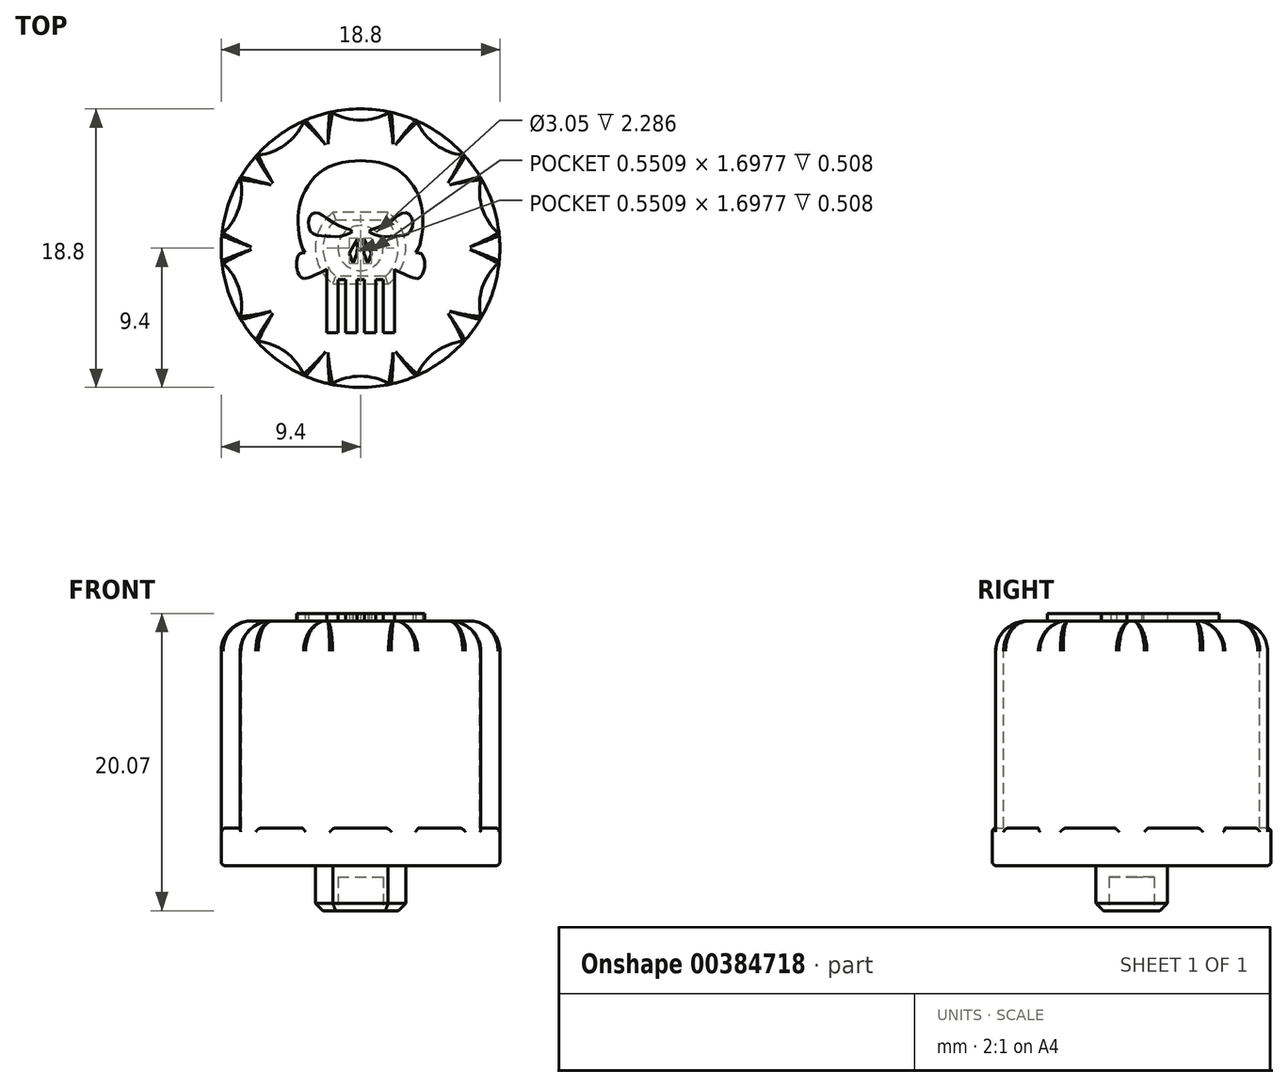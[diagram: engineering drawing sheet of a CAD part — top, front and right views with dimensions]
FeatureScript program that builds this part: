
annotation { "Feature Type Name" : "Feature", "Feature Type Description" : "" }
export const myFeature = defineFeature(function(context is Context, id is Id, definition is map)
    precondition{}
    {
        {
            var Q0;
            Q0=qCreatedBy(makeId("Top.planeOp"),FACE);
            var sketch = newSketch(context, id + "F0", { "sketchPlane" : qUnion([Q0])});
            skCircle(sketch, "E0", {"center": v(0, 0) * mm, "radius": 9.4 * mm});
            skSolve(sketch);
        }
        {
            var Q0;
            Q0=qSketchRegion(id+"F0",true);
            extrude(context, id + "F1", {"entities" : qUnion([Q0]), "depth" : 16.5 * mm});
        }
        {
            var Q0;
            Q0=makeQuery(id+"F1.opExtrude","CAP_FACE",FACE,{"disambiguationData":[OSD([sQuery(id+"F0.wireOp",EDGE,"E0")])],"isStart":false});
            var sketch = newSketch(context, id + "F2", { "sketchPlane" : qUnion([Q0])});
            skCircle(sketch, "E1.1.0", {"center": v(-7.32, 10.07) * mm, "radius": 3.81 * mm});
            skCircle(sketch, "E1.2.0", {"center": v(-11.84, 3.85) * mm, "radius": 3.81 * mm});
            skCircle(sketch, "E1.3.0", {"center": v(-11.84, -3.85) * mm, "radius": 3.81 * mm});
            skCircle(sketch, "E1.4.0", {"center": v(-7.32, -10.07) * mm, "radius": 3.81 * mm});
            skCircle(sketch, "E1.5.0", {"center": v(0, -12.45) * mm, "radius": 3.81 * mm});
            skCircle(sketch, "E1.6.0", {"center": v(7.32, -10.07) * mm, "radius": 3.81 * mm});
            skCircle(sketch, "E1.7.0", {"center": v(11.84, -3.85) * mm, "radius": 3.81 * mm});
            skCircle(sketch, "E1.8.0", {"center": v(11.84, 3.85) * mm, "radius": 3.81 * mm});
            skCircle(sketch, "E1.9.0", {"center": v(7.32, 10.07) * mm, "radius": 3.81 * mm});
            skPoint(sketch, "E1.center", {"position": v(0, 0) * mm});
            skPoint(sketch, "E2.center.orphan", {"position": v(0, 12.45) * mm});
            skCircle(sketch, "E3", {"center": v(0, 12.45) * mm, "radius": 3.81 * mm});
            skSolve(sketch);
        }
        {
            var Q0;
            Q0=qSketchRegion(id+"F2",true);
            extrude(context, id + "F3", {"entities" : qUnion([Q0]), "operationType" : NewBodyOperationType.REMOVE, "oppositeDirection" : true, "depth" : 13.97 * mm});
        }
        {
            var Q0;
            Q0=makeQuery(id+"F1.opExtrude","CAP_FACE",FACE,{"disambiguationData":[OSD([sQuery(id+"F0.wireOp",EDGE,"E0")])],"isStart":false});
            fillet(context, id + "F4", {"entities" : qUnion([Q0]), "radius" : 2.03 * mm, "tangentPropagation" : true, "allowEdgeOverflow" : false});
        }
        {
            var Q0;
            Q0=makeQuery(id+"F1.opExtrude","CAP_FACE",FACE,{"disambiguationData":[OSD([sQuery(id+"F0.wireOp",EDGE,"E0")])],"isStart":true});
            var sketch = newSketch(context, id + "F5", { "sketchPlane" : qUnion([Q0])});
            skCircle(sketch, "E4", {"center": v(0, 0) * mm, "radius": 5.33 * mm});
            skSolve(sketch);
        }
        {
            var Q0;
            Q0=qSketchRegion(id+"F5",true);
            extrude(context, id + "F6", {"entities" : qUnion([Q0]), "operationType" : NewBodyOperationType.ADD, "depth" : 8.25 * mm, "offsetDistance" : 25.4 * mm});
        }
        {
            var Q0;
            Q0=makeQuery(id+"F6.opExtrude","CAP_FACE",FACE,{"disambiguationData":[OSD([sQuery(id+"F5.wireOp",EDGE,"E4")])],"isStart":false});
            var sketch = newSketch(context, id + "F7", { "sketchPlane" : qUnion([Q0])});
            skCircle(sketch, "E5", {"center": v(0, 10.16) * mm, "radius": 5.72 * mm});
            skCircle(sketch, "E6.1.0", {"center": v(-9.66, 3.14) * mm, "radius": 5.72 * mm});
            skCircle(sketch, "E6.2.0", {"center": v(-5.97, -8.22) * mm, "radius": 5.72 * mm});
            skCircle(sketch, "E6.3.0", {"center": v(5.97, -8.22) * mm, "radius": 5.72 * mm});
            skCircle(sketch, "E6.4.0", {"center": v(9.66, 3.14) * mm, "radius": 5.72 * mm});
            skPoint(sketch, "E6.center", {"position": v(0, 0) * mm});
            skSolve(sketch);
        }
        {
            var Q0;
            Q0=qSketchRegion(id+"F7",true);
            extrude(context, id + "F8", {"entities" : qUnion([Q0]), "operationType" : NewBodyOperationType.REMOVE, "oppositeDirection" : true, "depth" : 7.62 * mm});
        }
        {
            var Q0;
            Q0=makeQuery(id+"F8.boolean.opBoolean","MERGE",FACE,{"derivedFrom":[makeQuery(id+"F1.opExtrude","CAP_FACE",FACE,{"disambiguationData":[OSD([sQuery(id+"F0.wireOp",EDGE,"E0")])],"isStart":true}),makeQuery(id+"F8.opExtrude","CAP_FACE",FACE,{"disambiguationData":[OSD([sQuery(id+"F7.wireOp",EDGE,"E5")])],"isStart":false}),makeQuery(id+"F8.opExtrude","CAP_FACE",FACE,{"disambiguationData":[OSD([sQuery(id+"F7.wireOp",EDGE,"E6.1.0")])],"isStart":false}),makeQuery(id+"F8.opExtrude","CAP_FACE",FACE,{"disambiguationData":[OSD([sQuery(id+"F7.wireOp",EDGE,"E6.2.0")])],"isStart":false}),makeQuery(id+"F8.opExtrude","CAP_FACE",FACE,{"disambiguationData":[OSD([sQuery(id+"F7.wireOp",EDGE,"E6.3.0")])],"isStart":false}),makeQuery(id+"F8.opExtrude","CAP_FACE",FACE,{"disambiguationData":[OSD([sQuery(id+"F7.wireOp",EDGE,"E6.4.0")])],"isStart":false})]});
            var sketch = newSketch(context, id + "F9", { "sketchPlane" : qUnion([Q0])});
            skCircle(sketch, "E7", {"center": v(0, 0) * mm, "radius": 6.22 * mm});
            skCircle(sketch, "E8", {"center": v(0, 0) * mm, "radius": 4.32 * mm});
            skSolve(sketch);
        }
        {
            var Q0;
            Q0=qSketchRegion(id+"F9",true);
            extrude(context, id + "F10", {"entities" : qUnion([Q0]), "operationType" : NewBodyOperationType.REMOVE, "depth" : 4.06 * mm, "offsetDistance" : 25.4 * mm});
        }
        {
            var Q0;
            Q0=makeQuery(id+"F10.boolean.opBoolean","MERGE",FACE,{"derivedFrom":[makeQuery(id+"F1.opExtrude","CAP_FACE",FACE,{"disambiguationData":[OSD([sQuery(id+"F0.wireOp",EDGE,"E0")])],"isStart":true}),makeQuery(id+"F10.opExtrude","CAP_FACE",FACE,{"disambiguationData":[OSD([sQuery(id+"F9.wireOp",EDGE,"E7"),sQuery(id+"F9.wireOp",EDGE,"E8")])],"isStart":true})]});
            var sketch = newSketch(context, id + "F11", { "sketchPlane" : qUnion([Q0])});
            skCircle(sketch, "E9", {"center": v(0, 0) * mm, "radius": 6.35 * mm});
            skSolve(sketch);
        }
        {
            var Q0;
            Q0=qSketchRegion(id+"F11",true);
            extrude(context, id + "F12", {"entities" : qUnion([Q0]), "operationType" : NewBodyOperationType.ADD, "depth" : 2.54 * mm, "offsetDistance" : 25.4 * mm});
        }
        {
            var Q0;
            Q0=makeQuery(id+"F6.opExtrude","CAP_FACE",FACE,{"disambiguationData":[OSD([sQuery(id+"F5.wireOp",EDGE,"E4")])],"isStart":false});
            fillet(context, id + "F13", {"entities" : qUnion([Q0]), "radius" : 0.5 * mm, "tangentPropagation" : true, "allowEdgeOverflow" : false});
        }
        {
            var Q0;
            Q0=makeQuery(id+"F12.opExtrude","CAP_EDGE",EDGE,{"disambiguationData":[OSD([sQuery(id+"F11.wireOp",EDGE,"E9")])],"isStart":false});
            var Q1;
            Q1=makeQuery(id+"F1.opExtrude","CAP_EDGE",EDGE,{"disambiguationData":[OSD([sQuery(id+"F0.wireOp",EDGE,"E0")])],"isStart":true});
            var Q2;
            Q2=makeQuery(id+"F3.boolean.opBoolean","INTERSECT",EDGE,{"derivedFrom":[makeQuery(id+"F1.opExtrude","SWEPT_FACE",FACE,{"disambiguationData":[OSD([sQuery(id+"F0.wireOp",EDGE,"E0")])]}),makeQuery(id+"F3.opExtrude","CAP_FACE",FACE,{"disambiguationData":[OSD([sQuery(id+"F2.wireOp",EDGE,"E1.4.0")])],"isStart":false})]});
            var Q3;
            Q3=makeQuery(id+"F3.boolean.opBoolean","INTERSECT",EDGE,{"derivedFrom":[makeQuery(id+"F1.opExtrude","SWEPT_FACE",FACE,{"disambiguationData":[OSD([sQuery(id+"F0.wireOp",EDGE,"E0")])]}),makeQuery(id+"F3.opExtrude","CAP_FACE",FACE,{"disambiguationData":[OSD([sQuery(id+"F2.wireOp",EDGE,"E1.5.0")])],"isStart":false})]});
            var Q4;
            Q4=makeQuery(id+"F3.boolean.opBoolean","INTERSECT",EDGE,{"disambiguationData":[OD(0.0)],"derivedFrom":[makeQuery(id+"F1.opExtrude","SWEPT_FACE",FACE,{"disambiguationData":[OSD([sQuery(id+"F0.wireOp",EDGE,"E0")])]}),makeQuery(id+"F3.opExtrude","SWEPT_FACE",FACE,{"disambiguationData":[OSD([sQuery(id+"F2.wireOp",EDGE,"E1.4.0")])]})]});
            var Q5;
            Q5=makeQuery(id+"F3.boolean.opBoolean","INTERSECT",EDGE,{"disambiguationData":[OD(1.0)],"derivedFrom":[makeQuery(id+"F1.opExtrude","SWEPT_FACE",FACE,{"disambiguationData":[OSD([sQuery(id+"F0.wireOp",EDGE,"E0")])]}),makeQuery(id+"F3.opExtrude","SWEPT_FACE",FACE,{"disambiguationData":[OSD([sQuery(id+"F2.wireOp",EDGE,"E1.4.0")])]})]});
            var Q6;
            Q6=makeQuery(id+"F3.boolean.opBoolean","INTERSECT",EDGE,{"disambiguationData":[OD(0.0)],"derivedFrom":[makeQuery(id+"F1.opExtrude","SWEPT_FACE",FACE,{"disambiguationData":[OSD([sQuery(id+"F0.wireOp",EDGE,"E0")])]}),makeQuery(id+"F3.opExtrude","SWEPT_FACE",FACE,{"disambiguationData":[OSD([sQuery(id+"F2.wireOp",EDGE,"E1.5.0")])]})]});
            var Q7;
            Q7=makeQuery(id+"F3.boolean.opBoolean","INTERSECT",EDGE,{"disambiguationData":[OD(1.0)],"derivedFrom":[makeQuery(id+"F1.opExtrude","SWEPT_FACE",FACE,{"disambiguationData":[OSD([sQuery(id+"F0.wireOp",EDGE,"E0")])]}),makeQuery(id+"F3.opExtrude","SWEPT_FACE",FACE,{"disambiguationData":[OSD([sQuery(id+"F2.wireOp",EDGE,"E1.5.0")])]})]});
            var Q8;
            Q8=makeQuery(id+"F3.boolean.opBoolean","INTERSECT",EDGE,{"disambiguationData":[OD(0.0)],"derivedFrom":[makeQuery(id+"F1.opExtrude","SWEPT_FACE",FACE,{"disambiguationData":[OSD([sQuery(id+"F0.wireOp",EDGE,"E0")])]}),makeQuery(id+"F3.opExtrude","SWEPT_FACE",FACE,{"disambiguationData":[OSD([sQuery(id+"F2.wireOp",EDGE,"E1.6.0")])]})]});
            var Q9;
            Q9=makeQuery(id+"F3.boolean.opBoolean","INTERSECT",EDGE,{"derivedFrom":[makeQuery(id+"F1.opExtrude","SWEPT_FACE",FACE,{"disambiguationData":[OSD([sQuery(id+"F0.wireOp",EDGE,"E0")])]}),makeQuery(id+"F3.opExtrude","CAP_FACE",FACE,{"disambiguationData":[OSD([sQuery(id+"F2.wireOp",EDGE,"E1.6.0")])],"isStart":false})]});
            var Q10;
            Q10=makeQuery(id+"F3.boolean.opBoolean","INTERSECT",EDGE,{"disambiguationData":[OD(1.0)],"derivedFrom":[makeQuery(id+"F1.opExtrude","SWEPT_FACE",FACE,{"disambiguationData":[OSD([sQuery(id+"F0.wireOp",EDGE,"E0")])]}),makeQuery(id+"F3.opExtrude","SWEPT_FACE",FACE,{"disambiguationData":[OSD([sQuery(id+"F2.wireOp",EDGE,"E1.6.0")])]})]});
            var Q11;
            Q11=makeQuery(id+"F3.boolean.opBoolean","INTERSECT",EDGE,{"disambiguationData":[OD(0.0)],"derivedFrom":[makeQuery(id+"F1.opExtrude","SWEPT_FACE",FACE,{"disambiguationData":[OSD([sQuery(id+"F0.wireOp",EDGE,"E0")])]}),makeQuery(id+"F3.opExtrude","SWEPT_FACE",FACE,{"disambiguationData":[OSD([sQuery(id+"F2.wireOp",EDGE,"E1.7.0")])]})]});
            var Q12;
            Q12=makeQuery(id+"F3.boolean.opBoolean","INTERSECT",EDGE,{"derivedFrom":[makeQuery(id+"F1.opExtrude","SWEPT_FACE",FACE,{"disambiguationData":[OSD([sQuery(id+"F0.wireOp",EDGE,"E0")])]}),makeQuery(id+"F3.opExtrude","CAP_FACE",FACE,{"disambiguationData":[OSD([sQuery(id+"F2.wireOp",EDGE,"E1.7.0")])],"isStart":false})]});
            var Q13;
            Q13=makeQuery(id+"F3.boolean.opBoolean","INTERSECT",EDGE,{"disambiguationData":[OD(1.0)],"derivedFrom":[makeQuery(id+"F1.opExtrude","SWEPT_FACE",FACE,{"disambiguationData":[OSD([sQuery(id+"F0.wireOp",EDGE,"E0")])]}),makeQuery(id+"F3.opExtrude","SWEPT_FACE",FACE,{"disambiguationData":[OSD([sQuery(id+"F2.wireOp",EDGE,"E1.7.0")])]})]});
            var Q14;
            Q14=makeQuery(id+"F3.boolean.opBoolean","INTERSECT",EDGE,{"derivedFrom":[makeQuery(id+"F1.opExtrude","SWEPT_FACE",FACE,{"disambiguationData":[OSD([sQuery(id+"F0.wireOp",EDGE,"E0")])]}),makeQuery(id+"F3.opExtrude","CAP_FACE",FACE,{"disambiguationData":[OSD([sQuery(id+"F2.wireOp",EDGE,"E1.8.0")])],"isStart":false})]});
            var Q15;
            Q15=makeQuery(id+"F3.boolean.opBoolean","INTERSECT",EDGE,{"disambiguationData":[OD(0.0)],"derivedFrom":[makeQuery(id+"F1.opExtrude","SWEPT_FACE",FACE,{"disambiguationData":[OSD([sQuery(id+"F0.wireOp",EDGE,"E0")])]}),makeQuery(id+"F3.opExtrude","SWEPT_FACE",FACE,{"disambiguationData":[OSD([sQuery(id+"F2.wireOp",EDGE,"E1.8.0")])]})]});
            var Q16;
            Q16=makeQuery(id+"F3.boolean.opBoolean","INTERSECT",EDGE,{"disambiguationData":[OD(1.0)],"derivedFrom":[makeQuery(id+"F1.opExtrude","SWEPT_FACE",FACE,{"disambiguationData":[OSD([sQuery(id+"F0.wireOp",EDGE,"E0")])]}),makeQuery(id+"F3.opExtrude","SWEPT_FACE",FACE,{"disambiguationData":[OSD([sQuery(id+"F2.wireOp",EDGE,"E1.8.0")])]})]});
            var Q17;
            Q17=makeQuery(id+"F3.boolean.opBoolean","INTERSECT",EDGE,{"disambiguationData":[OD(1.0)],"derivedFrom":[makeQuery(id+"F1.opExtrude","SWEPT_FACE",FACE,{"disambiguationData":[OSD([sQuery(id+"F0.wireOp",EDGE,"E0")])]}),makeQuery(id+"F3.opExtrude","SWEPT_FACE",FACE,{"disambiguationData":[OSD([sQuery(id+"F2.wireOp",EDGE,"E1.9.0")])]})]});
            var Q18;
            Q18=makeQuery(id+"F3.boolean.opBoolean","INTERSECT",EDGE,{"derivedFrom":[makeQuery(id+"F1.opExtrude","SWEPT_FACE",FACE,{"disambiguationData":[OSD([sQuery(id+"F0.wireOp",EDGE,"E0")])]}),makeQuery(id+"F3.opExtrude","CAP_FACE",FACE,{"disambiguationData":[OSD([sQuery(id+"F2.wireOp",EDGE,"E1.9.0")])],"isStart":false})]});
            var Q19;
            Q19=makeQuery(id+"F3.boolean.opBoolean","INTERSECT",EDGE,{"disambiguationData":[OD(0.0)],"derivedFrom":[makeQuery(id+"F1.opExtrude","SWEPT_FACE",FACE,{"disambiguationData":[OSD([sQuery(id+"F0.wireOp",EDGE,"E0")])]}),makeQuery(id+"F3.opExtrude","SWEPT_FACE",FACE,{"disambiguationData":[OSD([sQuery(id+"F2.wireOp",EDGE,"E1.9.0")])]})]});
            var Q20;
            Q20=makeQuery(id+"F3.boolean.opBoolean","INTERSECT",EDGE,{"disambiguationData":[OD(1.0)],"derivedFrom":[makeQuery(id+"F1.opExtrude","SWEPT_FACE",FACE,{"disambiguationData":[OSD([sQuery(id+"F0.wireOp",EDGE,"E0")])]}),makeQuery(id+"F3.opExtrude","SWEPT_FACE",FACE,{"disambiguationData":[OSD([sQuery(id+"F2.wireOp",EDGE,"E3")])]})]});
            var Q21;
            Q21=makeQuery(id+"F3.boolean.opBoolean","INTERSECT",EDGE,{"derivedFrom":[makeQuery(id+"F1.opExtrude","SWEPT_FACE",FACE,{"disambiguationData":[OSD([sQuery(id+"F0.wireOp",EDGE,"E0")])]}),makeQuery(id+"F3.opExtrude","CAP_FACE",FACE,{"disambiguationData":[OSD([sQuery(id+"F2.wireOp",EDGE,"E3")])],"isStart":false})]});
            var Q22;
            Q22=makeQuery(id+"F3.boolean.opBoolean","INTERSECT",EDGE,{"disambiguationData":[OD(0.0)],"derivedFrom":[makeQuery(id+"F1.opExtrude","SWEPT_FACE",FACE,{"disambiguationData":[OSD([sQuery(id+"F0.wireOp",EDGE,"E0")])]}),makeQuery(id+"F3.opExtrude","SWEPT_FACE",FACE,{"disambiguationData":[OSD([sQuery(id+"F2.wireOp",EDGE,"E3")])]})]});
            var Q23;
            Q23=makeQuery(id+"F3.boolean.opBoolean","INTERSECT",EDGE,{"derivedFrom":[makeQuery(id+"F1.opExtrude","SWEPT_FACE",FACE,{"disambiguationData":[OSD([sQuery(id+"F0.wireOp",EDGE,"E0")])]}),makeQuery(id+"F3.opExtrude","CAP_FACE",FACE,{"disambiguationData":[OSD([sQuery(id+"F2.wireOp",EDGE,"E1.1.0")])],"isStart":false})]});
            var Q24;
            Q24=makeQuery(id+"F3.boolean.opBoolean","INTERSECT",EDGE,{"disambiguationData":[OD(1.0)],"derivedFrom":[makeQuery(id+"F1.opExtrude","SWEPT_FACE",FACE,{"disambiguationData":[OSD([sQuery(id+"F0.wireOp",EDGE,"E0")])]}),makeQuery(id+"F3.opExtrude","SWEPT_FACE",FACE,{"disambiguationData":[OSD([sQuery(id+"F2.wireOp",EDGE,"E1.1.0")])]})]});
            var Q25;
            Q25=makeQuery(id+"F3.boolean.opBoolean","INTERSECT",EDGE,{"disambiguationData":[OD(0.0)],"derivedFrom":[makeQuery(id+"F1.opExtrude","SWEPT_FACE",FACE,{"disambiguationData":[OSD([sQuery(id+"F0.wireOp",EDGE,"E0")])]}),makeQuery(id+"F3.opExtrude","SWEPT_FACE",FACE,{"disambiguationData":[OSD([sQuery(id+"F2.wireOp",EDGE,"E1.1.0")])]})]});
            var Q26;
            Q26=makeQuery(id+"F3.boolean.opBoolean","INTERSECT",EDGE,{"disambiguationData":[OD(1.0)],"derivedFrom":[makeQuery(id+"F1.opExtrude","SWEPT_FACE",FACE,{"disambiguationData":[OSD([sQuery(id+"F0.wireOp",EDGE,"E0")])]}),makeQuery(id+"F3.opExtrude","SWEPT_FACE",FACE,{"disambiguationData":[OSD([sQuery(id+"F2.wireOp",EDGE,"E1.2.0")])]})]});
            var Q27;
            Q27=makeQuery(id+"F3.boolean.opBoolean","INTERSECT",EDGE,{"derivedFrom":[makeQuery(id+"F1.opExtrude","SWEPT_FACE",FACE,{"disambiguationData":[OSD([sQuery(id+"F0.wireOp",EDGE,"E0")])]}),makeQuery(id+"F3.opExtrude","CAP_FACE",FACE,{"disambiguationData":[OSD([sQuery(id+"F2.wireOp",EDGE,"E1.2.0")])],"isStart":false})]});
            var Q28;
            Q28=makeQuery(id+"F3.boolean.opBoolean","INTERSECT",EDGE,{"disambiguationData":[OD(0.0)],"derivedFrom":[makeQuery(id+"F1.opExtrude","SWEPT_FACE",FACE,{"disambiguationData":[OSD([sQuery(id+"F0.wireOp",EDGE,"E0")])]}),makeQuery(id+"F3.opExtrude","SWEPT_FACE",FACE,{"disambiguationData":[OSD([sQuery(id+"F2.wireOp",EDGE,"E1.2.0")])]})]});
            var Q29;
            Q29=makeQuery(id+"F3.boolean.opBoolean","INTERSECT",EDGE,{"disambiguationData":[OD(1.0)],"derivedFrom":[makeQuery(id+"F1.opExtrude","SWEPT_FACE",FACE,{"disambiguationData":[OSD([sQuery(id+"F0.wireOp",EDGE,"E0")])]}),makeQuery(id+"F3.opExtrude","SWEPT_FACE",FACE,{"disambiguationData":[OSD([sQuery(id+"F2.wireOp",EDGE,"E1.3.0")])]})]});
            var Q30;
            Q30=makeQuery(id+"F3.boolean.opBoolean","INTERSECT",EDGE,{"derivedFrom":[makeQuery(id+"F1.opExtrude","SWEPT_FACE",FACE,{"disambiguationData":[OSD([sQuery(id+"F0.wireOp",EDGE,"E0")])]}),makeQuery(id+"F3.opExtrude","CAP_FACE",FACE,{"disambiguationData":[OSD([sQuery(id+"F2.wireOp",EDGE,"E1.3.0")])],"isStart":false})]});
            var Q31;
            Q31=makeQuery(id+"F3.boolean.opBoolean","INTERSECT",EDGE,{"disambiguationData":[OD(0.0)],"derivedFrom":[makeQuery(id+"F1.opExtrude","SWEPT_FACE",FACE,{"disambiguationData":[OSD([sQuery(id+"F0.wireOp",EDGE,"E0")])]}),makeQuery(id+"F3.opExtrude","SWEPT_FACE",FACE,{"disambiguationData":[OSD([sQuery(id+"F2.wireOp",EDGE,"E1.3.0")])]})]});
            fillet(context, id + "F14", {"entities" : qUnion([Q0, Q1, Q2, Q3, Q4, Q5, Q6, Q7, Q8, Q9, Q10, Q11, Q12, Q13, Q14, Q15, Q16, Q17, Q18, Q19, Q20, Q21, Q22, Q23, Q24, Q25, Q26, Q27, Q28, Q29, Q30, Q31]), "radius" : 0.25 * mm, "tangentPropagation" : true, "allowEdgeOverflow" : false});
        }
        {
            var Q0;
            Q0=makeQuery(id+"F6.opExtrude","CAP_FACE",FACE,{"disambiguationData":[OSD([sQuery(id+"F5.wireOp",EDGE,"E4")])],"isStart":false});
            var sketch = newSketch(context, id + "F15", { "sketchPlane" : qUnion([Q0])});
            skCircle(sketch, "E10", {"center": v(0, 0) * mm, "radius": 1.52 * mm});
            skSolve(sketch);
        }
        {
            var Q0;
            Q0=qSketchRegion(id+"F15",true);
            extrude(context, id + "F16", {"entities" : qUnion([Q0]), "operationType" : NewBodyOperationType.REMOVE, "oppositeDirection" : true, "depth" : 7.37 * mm, "offsetDistance" : 25.4 * mm});
        }
        {
            var Q0;
            Q0=makeQuery(id+"F6.opExtrude","CAP_FACE",FACE,{"disambiguationData":[OSD([sQuery(id+"F5.wireOp",EDGE,"E4")])],"isStart":false});
            var sketch = newSketch(context, id + "F17", { "sketchPlane" : qUnion([Q0])});
            skArc(sketch, "E11", {"start": v(0.87, -2.92) * mm, "mid": v(0, 3.05) * mm, "end": v(-0.87, -2.92) * mm});
            skArc(sketch, "E12", {"start": v(-0.87, -2.92) * mm, "mid": v(0, -3.5) * mm, "end": v(0.87, -2.92) * mm});
            skCircle(sketch, "E13", {"center": v(0, 0) * mm, "radius": 1.52 * mm});
            skArc(sketch, "E14.1.0", {"start": v(0.87, 2.92) * mm, "mid": v(0, 3.5) * mm, "end": v(-0.87, 2.92) * mm});
            skSolve(sketch);
        }
        {
            var Q0;
            Q0=qSketchRegion(id+"F17",true);
            extrude(context, id + "F18", {"entities" : qUnion([Q0]), "operationType" : NewBodyOperationType.ADD, "depth" : 3.05 * mm, "offsetDistance" : 25.4 * mm});
        }
        {
            var Q0;
            Q0=makeQuery(id+"F18.opExtrude","CAP_FACE",FACE,{"disambiguationData":[OSD([sQuery(id+"F17.wireOp",EDGE,"E11"),sQuery(id+"F17.wireOp",EDGE,"E12"),sQuery(id+"F17.wireOp",EDGE,"E13")])],"isStart":false});
            fillet(context, id + "F19", {"entities" : qUnion([Q0]), "radius" : 0.5 * mm, "tangentPropagation" : true, "allowEdgeOverflow" : false});
        }
        {
            var Q0;
            Q0=makeQuery(id+"F10.boolean.opBoolean","MERGE",FACE,{"derivedFrom":[makeQuery(id+"F1.opExtrude","CAP_FACE",FACE,{"disambiguationData":[OSD([sQuery(id+"F0.wireOp",EDGE,"E0")])],"isStart":true}),makeQuery(id+"F10.opExtrude","CAP_FACE",FACE,{"disambiguationData":[OSD([sQuery(id+"F9.wireOp",EDGE,"E7"),sQuery(id+"F9.wireOp",EDGE,"E8")])],"isStart":true})]});
            var sketch = newSketch(context, id + "F20", { "sketchPlane" : qUnion([Q0])});
            skLineSegment(sketch, "E15.bottom", {"start": v(-12.19, 12.59) * mm, "end": v(12.3, 12.59) * mm});
            skLineSegment(sketch, "E15.top", {"start": v(-12.19, -14.05) * mm, "end": v(12.3, -14.05) * mm});
            skLineSegment(sketch, "E15.left", {"start": v(-12.19, 12.59) * mm, "end": v(-12.19, -14.05) * mm});
            skLineSegment(sketch, "E15.right", {"start": v(12.3, 12.59) * mm, "end": v(12.3, -14.05) * mm});
            skSolve(sketch);
        }
        {
            var Q0;
            Q0 = qSketchRegion(id + "F20", true);
            extrude(context, id + "F21", {"entities" : qUnion([Q0]), "operationType" : NewBodyOperationType.REMOVE, "depth" : 25.4 * mm, "offsetDistance" : 25.4 * mm});
        }
        {
            var Q0;
            Q0=makeQuery(id+"F21.boolean.opBoolean","MERGE",FACE,{"derivedFrom":[makeQuery(id+"F10.boolean.opBoolean","MERGE",FACE,{"derivedFrom":[makeQuery(id+"F1.opExtrude","CAP_FACE",FACE,{"disambiguationData":[OSD([sQuery(id+"F0.wireOp",EDGE,"E0")])],"isStart":true}),makeQuery(id+"F10.opExtrude","CAP_FACE",FACE,{"disambiguationData":[OSD([sQuery(id+"F9.wireOp",EDGE,"E7"),sQuery(id+"F9.wireOp",EDGE,"E8")])],"isStart":true})]}),makeQuery(id+"F21.opExtrude","CAP_FACE",FACE,{"disambiguationData":[OSD([sQuery(id+"F20.wireOp",EDGE,"E15.bottom"),sQuery(id+"F20.wireOp",EDGE,"E15.top"),sQuery(id+"F20.wireOp",EDGE,"E15.left"),sQuery(id+"F20.wireOp",EDGE,"E15.right")])],"isStart":true})]});
            var sketch = newSketch(context, id + "F22", { "sketchPlane" : qUnion([Q0])});
            skArc(sketch, "E16", {"start": v(-1.86, 2.41) * mm, "mid": v(-3.05, 0) * mm, "end": v(-1.86, -2.41) * mm});
            skLineSegment(sketch, "E17", {"start": v(-1.86, 2.41) * mm, "end": v(1.86, 2.41) * mm});
            skLineSegment(sketch, "E18", {"start": v(1.86, -2.41) * mm, "end": v(-1.86, -2.41) * mm});
            skArc(sketch, "E19.trimOffspring", {"start": v(1.86, -2.41) * mm, "mid": v(3.05, 0) * mm, "end": v(1.86, 2.41) * mm});
            skSolve(sketch);
        }
        {
            var Q0;
            Q0 = qSketchRegion(id + "F22", true);
            extrude(context, id + "F23", {"entities" : qUnion([Q0]), "operationType" : NewBodyOperationType.ADD, "depth" : 3.05 * mm, "offsetDistance" : 25.4 * mm});
        }
        {
            var Q0;
            Q0=makeQuery(id+"F23.opExtrude","CAP_FACE",FACE,{"disambiguationData":[OSD([sQuery(id+"F22.wireOp",EDGE,"E16"),sQuery(id+"F22.wireOp",EDGE,"E17"),sQuery(id+"F22.wireOp",EDGE,"E18"),sQuery(id+"F22.wireOp",EDGE,"E19.trimOffspring")])],"isStart":false});
            var sketch = newSketch(context, id + "F24", { "sketchPlane" : qUnion([Q0])});
            skCircle(sketch, "E20", {"center": v(0, 0) * mm, "radius": 1.52 * mm});
            skSolve(sketch);
        }
        {
            var Q0;
            Q0 = qSketchRegion(id + "F24", true);
            extrude(context, id + "F25", {"entities" : qUnion([Q0]), "operationType" : NewBodyOperationType.REMOVE, "oppositeDirection" : true, "depth" : 2.3 * mm, "offsetDistance" : 25.4 * mm});
        }
        {
            var Q0;
            Q0=makeQuery(id+"F1.opExtrude","CAP_FACE",FACE,{"disambiguationData":[OSD([sQuery(id+"F0.wireOp",EDGE,"E0")])],"isStart":false});
            var sketch = newSketch(context, id + "F26", { "sketchPlane" : qUnion([Q0])});
            skFitSpline(sketch, "E21", {"points": [v(0, 5.9) * mm, v(-2.18, 5.48) * mm, v(-3.55, 4.2) * mm, v(-4.14, 2.74) * mm, v(-4.14, 0.9) * mm, v(-3.74, -0.31) * mm], "startDerivative": vector(-7.73, 0.14) * mm, "endDerivative": vector(3.9, -5.46) * mm});
            skLineSegment(sketch, "E22", {"start": v(-2.29, -1.4) * mm, "end": v(-2.29, -5.7) * mm});
            skLineSegment(sketch, "E23", {"start": v(-2.29, -5.7) * mm, "end": v(-1.52, -5.7) * mm});
            skLineSegment(sketch, "E24", {"start": v(-0.25, -5.7) * mm, "end": v(-0.25, -2.13) * mm});
            skLineSegment(sketch, "E25", {"start": v(-1.02, -2.13) * mm, "end": v(-1.02, -5.7) * mm});
            skLineSegment(sketch, "E26", {"start": v(-1.52, -5.7) * mm, "end": v(-1.52, -2.13) * mm});
            skLineSegment(sketch, "E27", {"start": v(-1.52, -2.13) * mm, "end": v(-1.02, -2.13) * mm});
            skLineSegment(sketch, "E28.trimOffspring", {"start": v(-1.02, -5.7) * mm, "end": v(-0.25, -5.7) * mm});
            skPoint(sketch, "E29.1.internal.orphan", {"position": v(-3.6, -0.31) * mm});
            skPoint(sketch, "E29.5.internal.orphan", {"position": v(-2.29, -1.4) * mm});
            skFitSpline(sketch, "E30", {"points": [v(-3.74, -0.31) * mm, v(-4.08, -0.37) * mm, v(-4.3, -0.8) * mm, v(-4.28, -1.44) * mm, v(-3.97, -2) * mm, v(-3.41, -1.94) * mm, v(-2.29, -1.4) * mm], "startDerivative": vector(-2.83, -0.38) * mm, "endDerivative": vector(4.55, 3) * mm});
            skLineSegment(sketch, "E31", {"start": v(-0.25, -2.13) * mm, "end": v(0, -2.13) * mm});
            skLineSegment(sketch, "E32.MirrorCS", {"start": v(1.52, -2.13) * mm, "end": v(1.02, -2.13) * mm});
            skLineSegment(sketch, "E33.MirrorCS", {"start": v(1.02, -5.7) * mm, "end": v(0.25, -5.7) * mm});
            skLineSegment(sketch, "E34.MirrorCS", {"start": v(2.29, -5.7) * mm, "end": v(1.52, -5.7) * mm});
            skLineSegment(sketch, "E35.MirrorCS", {"start": v(0.25, -2.13) * mm, "end": v(0, -2.13) * mm});
            skFitSpline(sketch, "E36.MirrorCS", {"points": [v(3.74, -0.31) * mm, v(4.08, -0.37) * mm, v(4.3, -0.8) * mm, v(4.28, -1.44) * mm, v(3.97, -2) * mm, v(3.41, -1.94) * mm, v(2.29, -1.4) * mm], "startDerivative": vector(2.83, -0.38) * mm, "endDerivative": vector(-4.55, 3) * mm});
            skPoint(sketch, "E37.MirrorP", {"position": v(3.6, -0.31) * mm});
            skLineSegment(sketch, "E38.MirrorCS", {"start": v(1.02, -2.13) * mm, "end": v(1.02, -5.7) * mm});
            skLineSegment(sketch, "E39.MirrorCS", {"start": v(0.25, -5.7) * mm, "end": v(0.25, -2.13) * mm});
            skFitSpline(sketch, "E40.MirrorCS", {"points": [v(0, 5.9) * mm, v(2.18, 5.48) * mm, v(3.55, 4.2) * mm, v(4.14, 2.74) * mm, v(4.14, 0.9) * mm, v(3.74, -0.31) * mm], "startDerivative": vector(7.73, 0.14) * mm, "endDerivative": vector(-3.9, -5.46) * mm});
            skLineSegment(sketch, "E41.MirrorCS", {"start": v(1.52, -5.7) * mm, "end": v(1.52, -2.13) * mm});
            skLineSegment(sketch, "E42.MirrorCS", {"start": v(2.29, -1.4) * mm, "end": v(2.29, -5.7) * mm});
            skFitSpline(sketch, "E43", {"points": [v(-0.57, 1.13) * mm, v(-1.65, 1.61) * mm, v(-2.99, 2.4) * mm, v(-3.48, 1.97) * mm, v(-3.28, 1.03) * mm, v(-2.45, 0.82) * mm, v(-1.4, 0.81) * mm, v(-0.57, 1.13) * mm]});
            skLineSegment(sketch, "E44", {"start": v(-0.19, 0.67) * mm, "end": v(-0.74, -0.33) * mm});
            skLineSegment(sketch, "E45", {"start": v(-0.74, -0.33) * mm, "end": v(-0.5, -1.03) * mm});
            skLineSegment(sketch, "E46", {"start": v(-0.5, -1.03) * mm, "end": v(-0.23, -0.34) * mm});
            skLineSegment(sketch, "E47", {"start": v(-0.23, -0.34) * mm, "end": v(-0.19, 0.67) * mm});
            skLineSegment(sketch, "E48.MirrorCS", {"start": v(0.5, -1.03) * mm, "end": v(0.23, -0.34) * mm});
            skFitSpline(sketch, "E49.MirrorC", {"points": [v(0.57, 1.13) * mm, v(1.65, 1.61) * mm, v(2.99, 2.4) * mm, v(3.48, 1.97) * mm, v(3.28, 1.03) * mm, v(2.45, 0.82) * mm, v(1.4, 0.81) * mm, v(0.57, 1.13) * mm]});
            skLineSegment(sketch, "E50.MirrorCS", {"start": v(0.74, -0.33) * mm, "end": v(0.5, -1.03) * mm});
            skLineSegment(sketch, "E51.MirrorCS", {"start": v(0.19, 0.67) * mm, "end": v(0.74, -0.33) * mm});
            skLineSegment(sketch, "E52.MirrorCS", {"start": v(0.23, -0.34) * mm, "end": v(0.19, 0.67) * mm});
            skSolve(sketch);
        }
        {
            var Q0;
            Q0 = qSketchRegion(id + "F26", true);
            extrude(context, id + "F27", {"entities" : qUnion([Q0]), "operationType" : NewBodyOperationType.ADD, "depth" : 0.5 * mm, "offsetDistance" : 25.4 * mm});
        }
        {
            var Q0;
            Q0=makeQuery(id+"F23.opExtrude","CAP_EDGE",EDGE,{"disambiguationData":[OSD([sQuery(id+"F22.wireOp",EDGE,"E18")])],"isStart":false});
            var Q1;
            Q1=makeQuery(id+"F23.opExtrude","CAP_EDGE",EDGE,{"disambiguationData":[OSD([sQuery(id+"F22.wireOp",EDGE,"E19.trimOffspring")])],"isStart":false});
            var Q2;
            Q2=makeQuery(id+"F23.opExtrude","CAP_EDGE",EDGE,{"disambiguationData":[OSD([sQuery(id+"F22.wireOp",EDGE,"E16")])],"isStart":false});
            var Q3;
            Q3=makeQuery(id+"F23.opExtrude","CAP_EDGE",EDGE,{"disambiguationData":[OSD([sQuery(id+"F22.wireOp",EDGE,"E17")])],"isStart":false});
            chamfer(context, id + "F28", {"entities" : qUnion([Q0, Q1, Q2, Q3]), "width" : 0.5 * mm, "tangentPropagation" : true});
        }
    });
